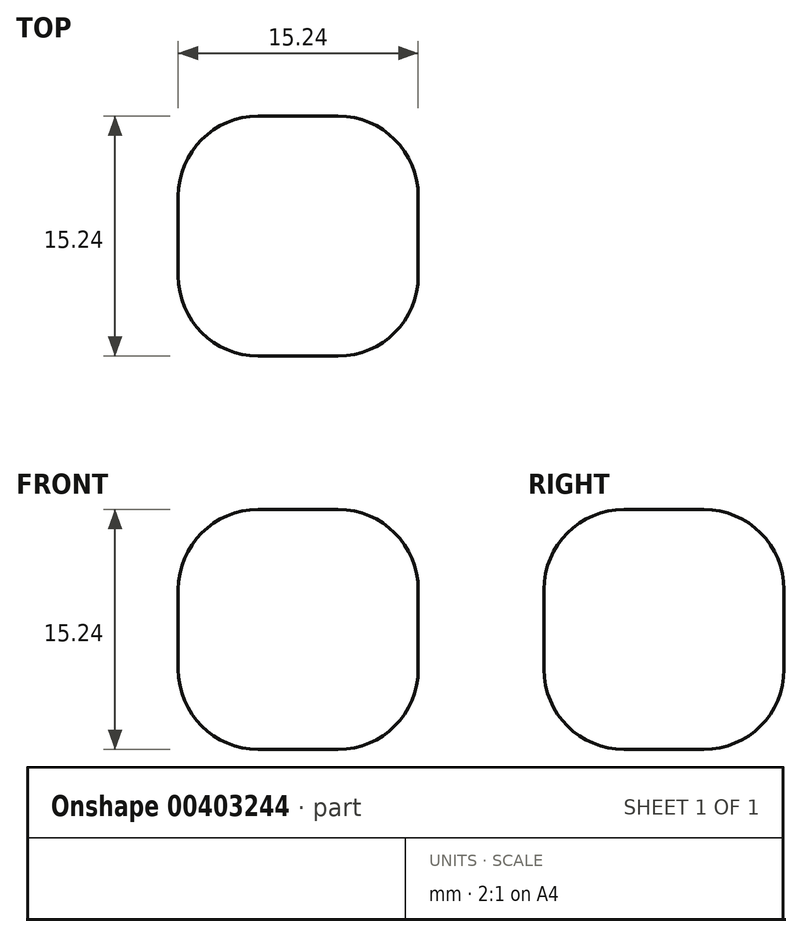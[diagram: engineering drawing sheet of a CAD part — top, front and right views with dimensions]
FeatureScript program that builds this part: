
annotation { "Feature Type Name" : "Feature", "Feature Type Description" : "" }
export const myFeature = defineFeature(function(context is Context, id is Id, definition is map)
    precondition{}
    {
        {
            var Q0;
            Q0=qCreatedBy(makeId("Top.planeOp"),FACE);
            var sketch = newSketch(context, id + "F0", { "sketchPlane" : qUnion([Q0])});
            skLineSegment(sketch, "E0.bottom", {"start": v(-21.57, 23.99) * mm, "end": v(-6.33, 23.99) * mm});
            skLineSegment(sketch, "E0.top", {"start": v(-21.57, 8.75) * mm, "end": v(-6.33, 8.75) * mm});
            skLineSegment(sketch, "E0.left", {"start": v(-21.57, 23.99) * mm, "end": v(-21.57, 8.75) * mm});
            skLineSegment(sketch, "E0.right", {"start": v(-6.33, 23.99) * mm, "end": v(-6.33, 8.75) * mm});
            skSolve(sketch);
        }
        {
            var Q0;
            Q0=makeQuery(id+"F0.imprint","IMPRINT",FACE,{"disambiguationData":[TD([[makeQuery(id+"F0.imprint","IMPRINT",EDGE,{"derivedFrom":sQuery(id+"F0.wireOp",EDGE,"E0.bottom")}),-1.0]])]});
            extrude(context, id + "F1", {"entities" : qUnion([Q0]), "depth" : 15.24 * mm});
        }
        {
            var Q0;
            Q0=makeQuery(id+"F1.opExtrude","CAP_FACE",FACE,{"disambiguationData":[OSD([sQuery(id+"F0.wireOp",EDGE,"E0.bottom"),sQuery(id+"F0.wireOp",EDGE,"E0.top"),sQuery(id+"F0.wireOp",EDGE,"E0.left"),sQuery(id+"F0.wireOp",EDGE,"E0.right")])],"isStart":false});
            var Q1;
            Q1=makeQuery(id+"F1.opExtrude","SWEPT_FACE",FACE,{"disambiguationData":[OSD([sQuery(id+"F0.wireOp",EDGE,"E0.bottom")])]});
            var Q2;
            Q2=makeQuery(id+"F1.opExtrude","SWEPT_FACE",FACE,{"disambiguationData":[OSD([sQuery(id+"F0.wireOp",EDGE,"E0.left")])]});
            var Q3;
            Q3=makeQuery(id+"F1.opExtrude","CAP_FACE",FACE,{"disambiguationData":[OSD([sQuery(id+"F0.wireOp",EDGE,"E0.bottom"),sQuery(id+"F0.wireOp",EDGE,"E0.top"),sQuery(id+"F0.wireOp",EDGE,"E0.left"),sQuery(id+"F0.wireOp",EDGE,"E0.right")])],"isStart":true});
            var Q4;
            Q4=makeQuery(id+"F1.opExtrude","SWEPT_FACE",FACE,{"disambiguationData":[OSD([sQuery(id+"F0.wireOp",EDGE,"E0.right")])]});
            fillet(context, id + "F2", {"entities" : qUnion([Q0, Q1, Q2, Q3, Q4]), "radius" : 5.08 * mm, "tangentPropagation" : true, "allowEdgeOverflow" : false});
        }
    });
